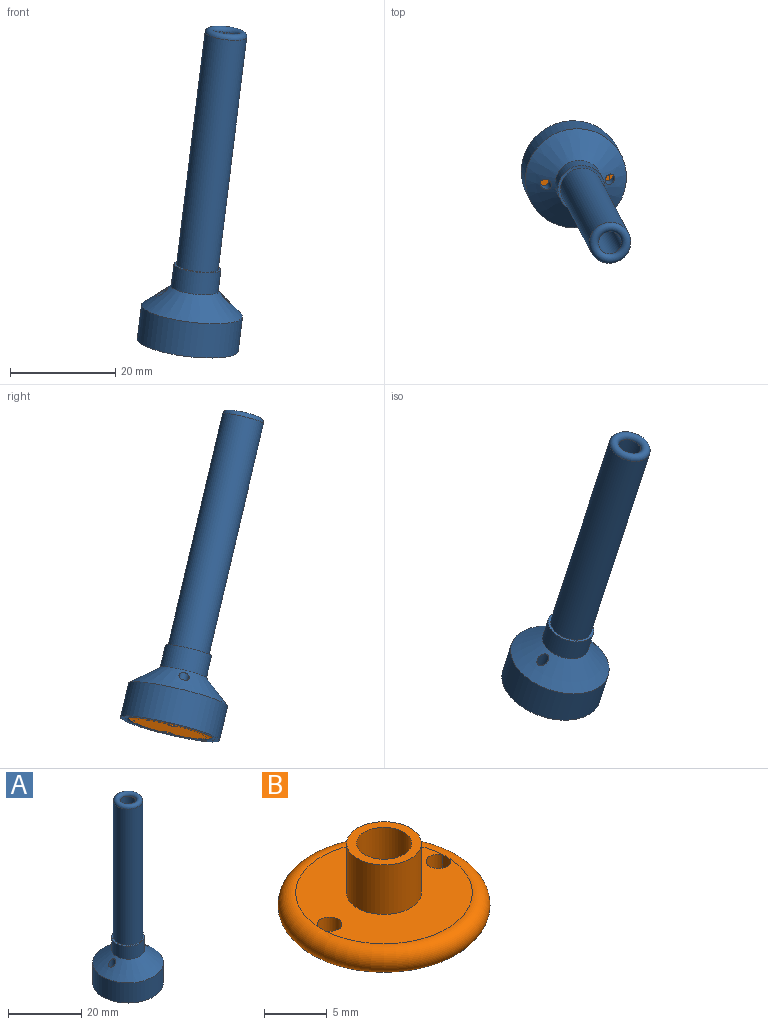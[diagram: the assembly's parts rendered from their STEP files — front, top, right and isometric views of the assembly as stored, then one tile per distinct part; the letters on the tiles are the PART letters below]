
ASSEMBLY  parts=2 mates=1
PART A: 16 faces, bbox 19.3x19.3x61.9 mm
  f0: cone r=9.66mm half-angle=50.1deg, axis (0,0,-1), area 291.6mm2, adj f3,f4,f14,f15
  f1: plane 16.28x16.28mm, normal (0,0,-1), area 174mm2, adj f10,f11,f14,f15
  f2: plane 19.33x19.33mm, normal (0,0,-1), area 58.5mm2, adj f3,f13
  f3: cylinder r=9.66mm len=19.33mm, axis (0,0,1), area 408.7mm2, adj f0,f2
  f4: cylinder r=4.5mm len=8.99mm, axis (0,0,1), area 122mm2, adj f0,f5
  f5: plane 8.99x8.99mm, normal (0,0,1), area 13.5mm2, adj f4,f6
  f6: cylinder r=3.99mm len=45.59mm, axis (0,0,1), area 1142.4mm2, adj f5,f7
  f7: torus R=3.09mm, axis (0,0,1), area 54.9mm2, adj f6,f8
  f8: cylinder r=2.18mm len=48.13mm, axis (0,0,1), area 660.6mm2, adj f7,f9
  f9: plane 5.97x5.97mm, normal (0,0,-1), area 13mm2, adj f8,f10
  f10: cylinder r=2.98mm len=6.35mm, axis (0,0,1), area 119.1mm2, adj f1,f9
  f11: torus R=8.14mm, axis (0,0,1), area 42.4mm2, adj f1,f12
  f12: cylinder r=8.65mm len=17.3mm, axis (0,0,1), area 268.8mm2, adj f11,f13
  f13: torus R=8.65mm, axis (0,0,1), area 83.7mm2, adj f2,f12
  f14: cylinder r=0.99mm len=4.03mm, axis (0,0,-1), area 19.7mm2, adj f0,f1
  f15: cylinder r=0.99mm len=4.03mm, axis (0,0,-1), area 19.7mm2, adj f0,f1
PART B: 11 faces, bbox 18.3x18.3x7.2 mm
  f0: plane 14.08x14.06mm, normal (0,0,-1), area 149.7mm2, adj f2,f8,f9
  f1: plane 14.08x14.06mm, normal (0,0,1), area 121.7mm2, adj f2,f3,f8,f9
  f2: torus R=7.26mm, axis (0,0,1), area 207.5mm2, adj f0,f1,f7,f10
  f3: cylinder r=2.98mm len=5.97mm, axis (0,0,1), area 90.5mm2, adj f1,f4
  f4: plane 5.97x5.97mm, normal (0,0,1), area 12.8mm2, adj f3,f5
  f5: cylinder r=2.2mm len=4.83mm, axis (0,0,1), area 66.6mm2, adj f4,f6
  f6: plane 4.39x4.39mm, normal (0,0,1), area 15.2mm2, adj f5
  f7: cylinder r=7.04mm len=2.34mm, axis (0,0,1), area 2mm2, adj f2,f8
  f8: cylinder r=0.99mm len=2.34mm, axis (0,0,1), area 12.5mm2, adj f0,f1,f7
  f9: cylinder r=0.99mm len=2.34mm, axis (0,0,1), area 12.5mm2, adj f0,f1,f10
  f10: cylinder r=7.04mm len=2.34mm, axis (0,0,1), area 2mm2, adj f2,f9
PLACE A rot(axis=(0.87,0.42,0.24),15.3deg) t=(-16.69,-5.14,8.33)mm
PLACE B rot(axis=(0.88,0.43,0.2),15.1deg) t=(-16.69,-5.14,8.33)mm
MATE cylindrical B.f3 <-> A.f0  axis (-0.12,0.23,-0.97) through (-16.69,-5.14,8.33)mm
